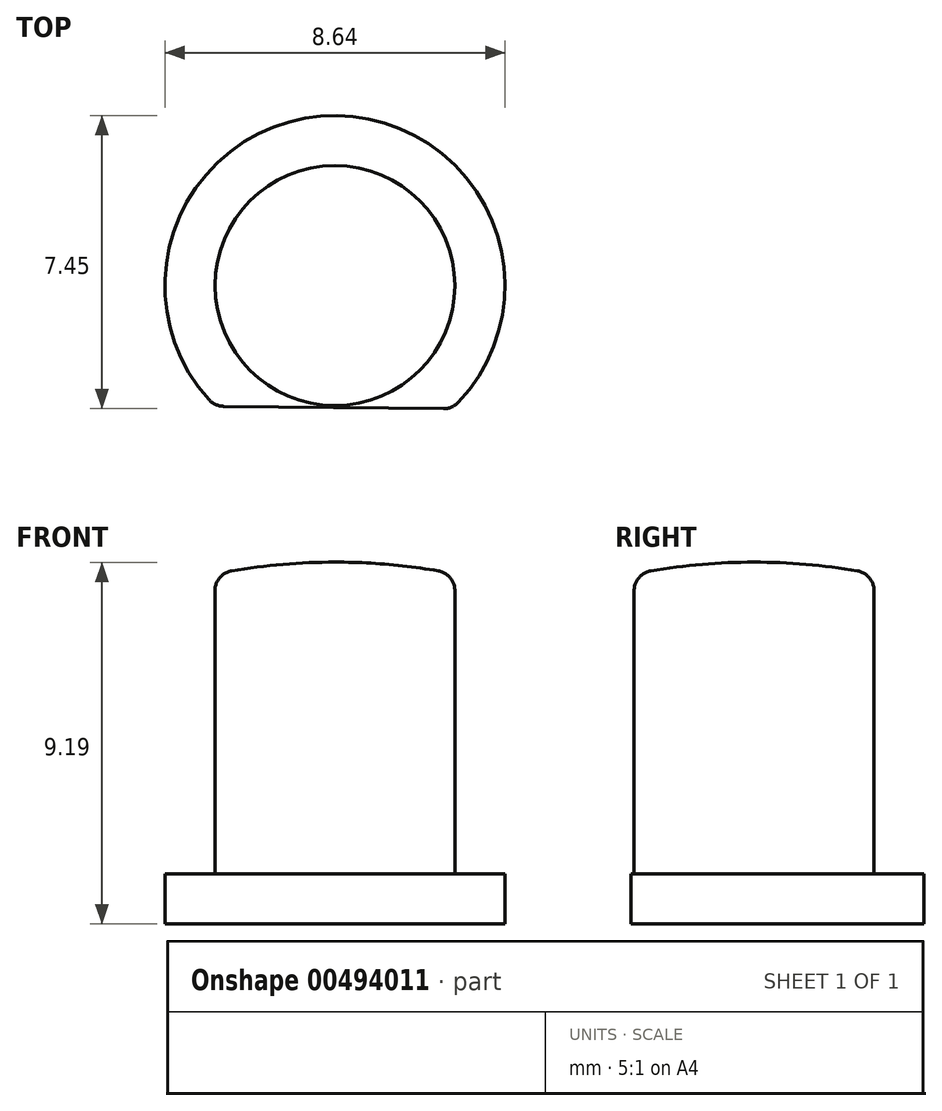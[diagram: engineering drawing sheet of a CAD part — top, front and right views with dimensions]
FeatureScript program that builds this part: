
annotation { "Feature Type Name" : "Feature", "Feature Type Description" : "" }
export const myFeature = defineFeature(function(context is Context, id is Id, definition is map)
    precondition{}
    {
        {
            var Q0;
            Q0=qCreatedBy(makeId("Front.planeOp"),FACE);
            var sketch = newSketch(context, id + "F0", { "sketchPlane" : qUnion([Q0])});
            skLineSegment(sketch, "E0", {"start": v(-3.05, 0) * mm, "end": v(-3.05, -7.62) * mm});
            skLineSegment(sketch, "E1", {"start": v(-3.05, -7.62) * mm, "end": v(-4.32, -7.62) * mm});
            skLineSegment(sketch, "E2", {"start": v(-4.32, -7.62) * mm, "end": v(-4.32, -8.89) * mm});
            skLineSegment(sketch, "E3", {"start": v(-4.32, -8.89) * mm, "end": v(0, -8.89) * mm});
            skArc(sketch, "E4", {"start": v(0, 0.3) * mm, "mid": v(-1.53, 0.23) * mm, "end": v(-3.05, 0) * mm});
            skLineSegment(sketch, "E5", {"start": v(0, 0.3) * mm, "end": v(0, -8.89) * mm});
            skSolve(sketch);
        }
        {
            var Q0;
            Q0 = qSketchRegion(id + "F0", true);
            var Q1;
            Q1=sQuery(id+"F0.wireOp",EDGE,"E5");
            revolve(context, id + "F1", {"entities" : qUnion([Q0]), "axis" : qUnion([Q1]), "revolveType" : RevolveType.FULL});
        }
        {
            var Q0;
            Q0=makeQuery(id+"F1.opRevolve","SWEPT_FACE",FACE,{"disambiguationData":[OSD([sQuery(id+"F0.wireOp",EDGE,"E1")])]});
            var sketch = newSketch(context, id + "F2", { "sketchPlane" : qUnion([Q0])});
            skLineSegment(sketch, "E6", {"start": v(-6.08, -3.03) * mm, "end": v(-6.08, -7.56) * mm});
            skLineSegment(sketch, "E7", {"start": v(-6.08, -7.56) * mm, "end": v(6.7, -7.56) * mm});
            skLineSegment(sketch, "E8", {"start": v(6.7, -7.56) * mm, "end": v(6.7, -3.17) * mm});
            skLineSegment(sketch, "E9", {"start": v(-6.08, -3.03) * mm, "end": v(6.7, -3.17) * mm});
            skSolve(sketch);
        }
        {
            var Q0;
            Q0 = qSketchRegion(id + "F2", true);
            extrude(context, id + "F3", {"entities" : qUnion([Q0]), "operationType" : NewBodyOperationType.REMOVE, "oppositeDirection" : true, "depth" : 25.4 * mm});
        }
        {
            var Q0;
            Q0=makeQuery(id+"F1.opRevolve","SWEPT_EDGE",EDGE,{"disambiguationData":[OSD([sQuery(id+"F0.wireOp",EDGE,"E0"),sQuery(id+"F0.wireOp",EDGE,"E4")])]});
            var Q1;
            Q1=makeQuery(id+"F3.boolean.opBoolean","INTERSECT",EDGE,{"disambiguationData":[OD(1.0)],"derivedFrom":[makeQuery(id+"F1.opRevolve","SWEPT_FACE",FACE,{"disambiguationData":[OSD([sQuery(id+"F0.wireOp",EDGE,"E2")])]}),makeQuery(id+"F3.opExtrude","SWEPT_FACE",FACE,{"disambiguationData":[OSD([sQuery(id+"F2.wireOp",EDGE,"E9")])]})]});
            var Q2;
            Q2=makeQuery(id+"F3.boolean.opBoolean","INTERSECT",EDGE,{"disambiguationData":[OD(0.0)],"derivedFrom":[makeQuery(id+"F1.opRevolve","SWEPT_FACE",FACE,{"disambiguationData":[OSD([sQuery(id+"F0.wireOp",EDGE,"E2")])]}),makeQuery(id+"F3.opExtrude","SWEPT_FACE",FACE,{"disambiguationData":[OSD([sQuery(id+"F2.wireOp",EDGE,"E9")])]})]});
            fillet(context, id + "F4", {"entities" : qUnion([Q0, Q1, Q2]), "radius" : 0.5 * mm, "tangentPropagation" : true, "allowEdgeOverflow" : false});
        }
    });
